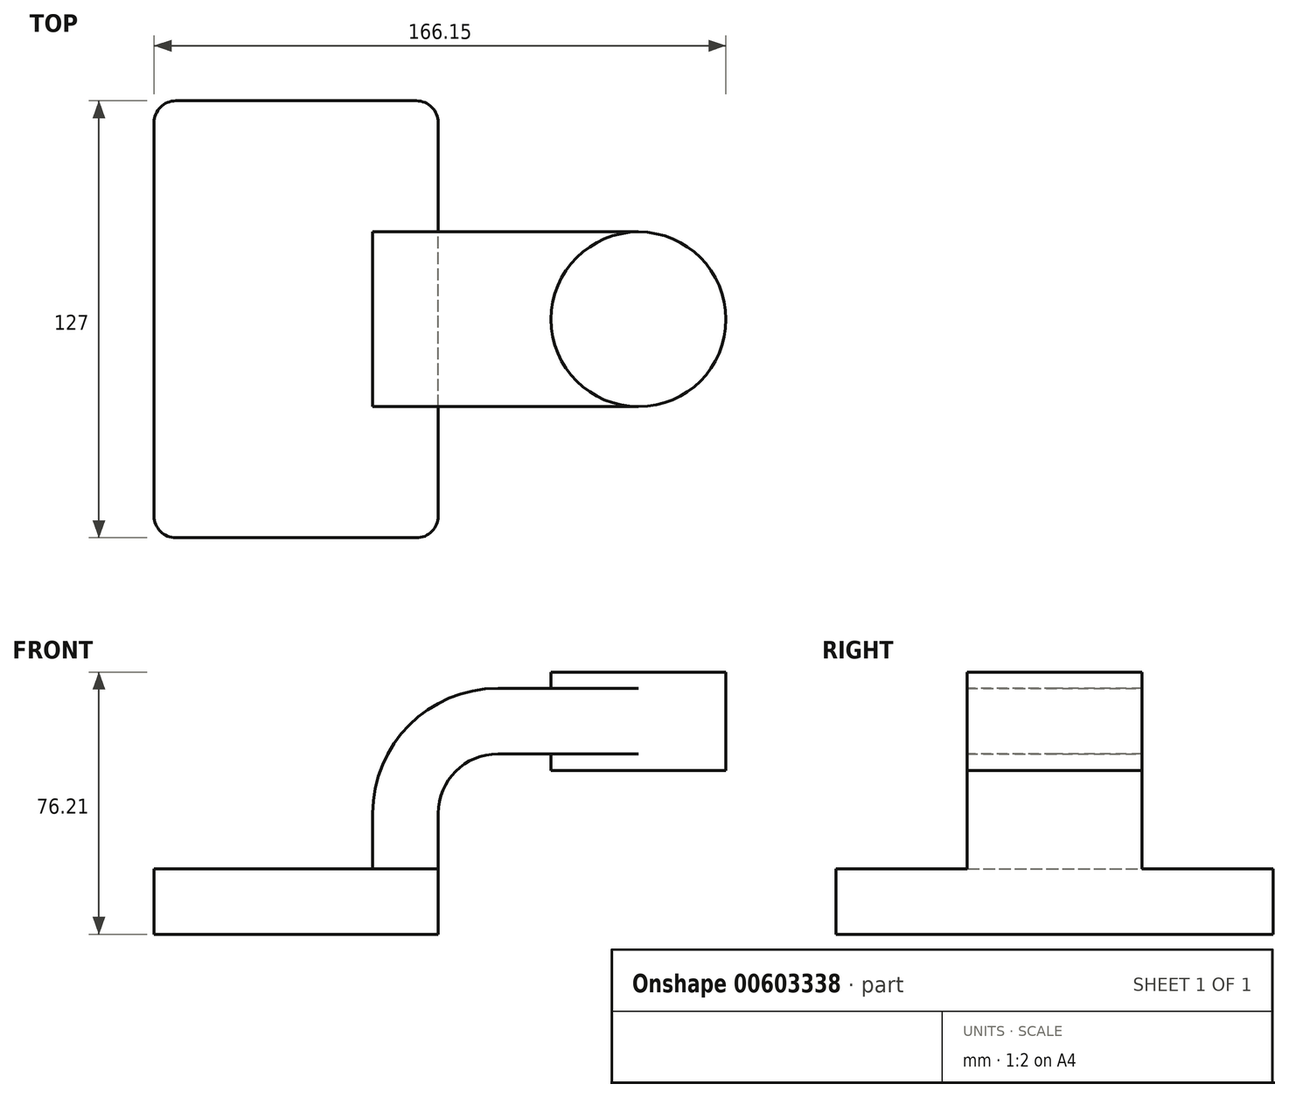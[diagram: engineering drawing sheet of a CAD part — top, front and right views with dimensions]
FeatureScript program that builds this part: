
annotation { "Feature Type Name" : "Feature", "Feature Type Description" : "" }
export const myFeature = defineFeature(function(context is Context, id is Id, definition is map)
    precondition{}
    {
        {
            var Q0;
            Q0=qCreatedBy(makeId("Front.planeOp"),FACE);
            var sketch = newSketch(context, id + "F0", { "sketchPlane" : qUnion([Q0])});
            skLineSegment(sketch, "E0.bottom", {"start": v(-41.28, 9.52) * mm, "end": v(41.27, 9.53) * mm});
            skLineSegment(sketch, "E0.top", {"start": v(-41.28, -9.52) * mm, "end": v(41.28, -9.52) * mm});
            skLineSegment(sketch, "E0.left", {"start": v(-41.28, 9.52) * mm, "end": v(-41.28, -9.53) * mm});
            skLineSegment(sketch, "E0.right", {"start": v(41.27, 9.53) * mm, "end": v(41.28, -9.52) * mm});
            skPoint(sketch, "E0.middle", {"position": v(0, 0) * mm});
            skLineSegment(sketch, "E1.bottom", {"start": v(74.08, 66.67) * mm, "end": v(124.88, 66.67) * mm});
            skLineSegment(sketch, "E1.top", {"start": v(74.08, 38.1) * mm, "end": v(124.88, 38.1) * mm});
            skLineSegment(sketch, "E1.left", {"start": v(74.08, 66.67) * mm, "end": v(74.08, 38.1) * mm});
            skLineSegment(sketch, "E1.right", {"start": v(124.88, 66.67) * mm, "end": v(124.88, 38.1) * mm});
            skPoint(sketch, "E1.middle", {"position": v(99.48, 52.39) * mm});
            skLineSegment(sketch, "E2", {"start": v(41.27, 9.53) * mm, "end": v(41.27, 25.55) * mm});
            skArc(sketch, "E3", {"start": v(41.28, 25.55) * mm, "mid": v(46.35, 37.8) * mm, "end": v(58.6, 42.88) * mm});
            skLineSegment(sketch, "E4", {"start": v(58.6, 42.88) * mm, "end": v(99.48, 42.88) * mm});
            skLineSegment(sketch, "E5.0", {"start": v(58.6, 61.93) * mm, "end": v(99.48, 61.93) * mm});
            skArc(sketch, "E5.1", {"start": v(22.23, 25.55) * mm, "mid": v(32.88, 51.27) * mm, "end": v(58.6, 61.93) * mm});
            skLineSegment(sketch, "E5.2", {"start": v(22.22, 9.53) * mm, "end": v(22.22, 25.55) * mm});
            skLineSegment(sketch, "E6", {"start": v(99.48, 38.1) * mm, "end": v(99.48, 66.67) * mm});
            skFitSpline(sketch, "E7", {"points": [v(-41.28, 9.52) * mm, v(58.6, 61.93) * mm], "startDerivative": vector(2.23, 97.09) * mm, "endDerivative": vector(107.58, -0.46) * mm});
            skSolve(sketch);
        }
        {
            var Q0;
            Q0=makeQuery(id+"F0.imprint","IMPRINT",FACE,{"disambiguationData":[TD([[makeQuery(id+"F0.imprint","IMPRINT",EDGE,{"derivedFrom":sQuery(id+"F0.wireOp",EDGE,"E0.top")}),1.0]])]});
            extrude(context, id + "F1", {"entities" : qUnion([Q0]), "endBound" : BoundingType.SYMMETRIC, "depth" : 127 * mm, "offsetDistance" : 25.4 * mm});
        }
        {
            var Q0;
            {var subQ1=sQuery(id+"F0.wireOp",EDGE,"E2");Q0=makeQuery(id+"F0.imprint","IMPRINT",FACE,{"disambiguationData":[TD([[makeQuery(id+"F0.imprint","IMPRINT",EDGE,{"derivedFrom":subQ1}),1.0]])]});}
            var Q1;
            {var subQ0=sQuery(id+"F0.wireOp",EDGE,"E5.0");var subQ1=sQuery(id+"F0.wireOp",EDGE,"E1.left");var subQ2=makeQuery(id+"F0.imprint","INTERSECT",VERTEX,{"derivedFrom":[subQ1,subQ0]});Q1=makeQuery(id+"F0.imprint","IMPRINT",FACE,{"disambiguationData":[TD([[makeQuery(id+"F0.imprint","IMPRINT",EDGE,{"disambiguationData":[TD([[subQ2,-1.0]])],"derivedFrom":subQ1}),1.0]])]});}
            extrude(context, id + "F2", {"entities" : qUnion([Q0, Q1]), "operationType" : NewBodyOperationType.ADD, "endBound" : BoundingType.SYMMETRIC, "depth" : 50.8 * mm, "offsetDistance" : 25.4 * mm});
        }
        {
            var Q0;
            Q0=makeQuery(id+"F0.imprint","IMPRINT",FACE,{"disambiguationData":[TD([[makeQuery(id+"F0.imprint","IMPRINT",EDGE,{"derivedFrom":sQuery(id+"F0.wireOp",EDGE,"E5.1")}),1.0]])]});
            extrude(context, id + "F3", {"entities" : qUnion([Q0]), "operationType" : NewBodyOperationType.ADD, "endBound" : BoundingType.SYMMETRIC, "depth" : 15.88 * mm, "offsetDistance" : 25.4 * mm});
        }
        {
            var Q0;
            {var subQ0=sQuery(id+"F0.wireOp",EDGE,"E1.right");Q0=makeQuery(id+"F0.imprint","IMPRINT",FACE,{"disambiguationData":[TD([[makeQuery(id+"F0.imprint","IMPRINT",EDGE,{"derivedFrom":subQ0}),-1.0]])]});}
            var Q1;
            Q1=sQuery(id+"F0.wireOp",EDGE,"E6");
            revolve(context, id + "F4", {"operationType" : NewBodyOperationType.ADD, "entities" : qUnion([Q0]), "axis" : qUnion([Q1]), "revolveType" : RevolveType.FULL});
        }
        {
            var Q0;
            Q0=makeQuery(id+"F1.opExtrude","CAP_EDGE",EDGE,{"disambiguationData":[OSD([sQuery(id+"F0.wireOp",EDGE,"E0.right")])],"isStart":false});
            var Q1;
            Q1=makeQuery(id+"F1.opExtrude","CAP_EDGE",EDGE,{"disambiguationData":[OSD([sQuery(id+"F0.wireOp",EDGE,"E0.left")])],"isStart":false});
            var Q2;
            Q2=makeQuery(id+"F1.opExtrude","CAP_EDGE",EDGE,{"disambiguationData":[OSD([sQuery(id+"F0.wireOp",EDGE,"E0.right")])],"isStart":true});
            var Q3;
            Q3=makeQuery(id+"F1.opExtrude","CAP_EDGE",EDGE,{"disambiguationData":[OSD([sQuery(id+"F0.wireOp",EDGE,"E0.left")])],"isStart":true});
            fillet(context, id + "F5", {"entities" : qUnion([Q0, Q1, Q2, Q3]), "radius" : 6.35 * mm, "tangentPropagation" : true, "allowEdgeOverflow" : false});
        }
    });
